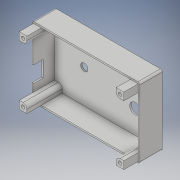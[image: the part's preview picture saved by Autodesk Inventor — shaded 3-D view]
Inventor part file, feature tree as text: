
AUTODESK INVENTOR PART (.ipt)
format: ipt  version: 2019 (Build 230136000, 136)  size: 409,088 bytes
history: native  units: mm
features: other x8, extrude x5, hole x1, fillet x1, loft x1, sketch x1
ambient origin geometry x8: Origin, YZ Plane, XZ Plane, XY Plane, X Axis, Y Axis, Z Axis, Center Point
bodies: Solid1 (feature_tree)
feature tree (17):
  extrude  "Extrusion1"  Depth=70.0mm
  other  "stena_RJ45"
  extrude  "Extrusion2"  Depth=1.2mm TaperAngle=0.0deg
  extrude  "Extrusion3"  Depth=1.6mm
  extrude  "Extrusion4"  Depth=16.8mm
  extrude  "Extrusion5"  Depth=15.7mm
  hole  "Hole1"  [1 undecoded]
  fillet  "Fillet1"  Radius=11.5mm
  other  "znacka_napajeni1"
  other  "rovina_napajeni_znacka2"
  loft  "Loft1"
  other  "zakladna"
  other  "diry_tlacirka_LED"
  other  "steny"
  sketch  "Sketch5"  dims[d0=109.0mm d1=70.0mm d2=1.2mm d3=0.0mm d4=1.6mm d5=16.8mm d6=15.7mm d7=0.0mm d9=11.5mm d10=7.7mm d11=31.0mm d12=2.0mm d13=0.0mm d18=23.4mm d19=0.0mm d20=13.6mm d21=0.0mm d22=8.0mm d27=36.8mm d28=0.0mm d29=3.3mm d30=6.0mm d31=3.65mm d32=2.0mm d33=1.396263mm d34=12.0mm d35=0.0mm d36=0.4mm d37=0.0mm d42=1.6mm d43=2.0mm d44=0.8mm d45=1.0mm d46=18.0mm d47=-0.5mm d48=0.0mm d49=90.0deg d50=0.0mm d51=90.0deg d53=25.0mm]
  other  "diry_zavitova_vlozka"
  other  "napajeni_znacka2"
note: 1 required parameter value undecoded (feature->parameter linkage not recoverable at this tier; creation-order binding heuristic only, values carry confidence <= 0.55)
